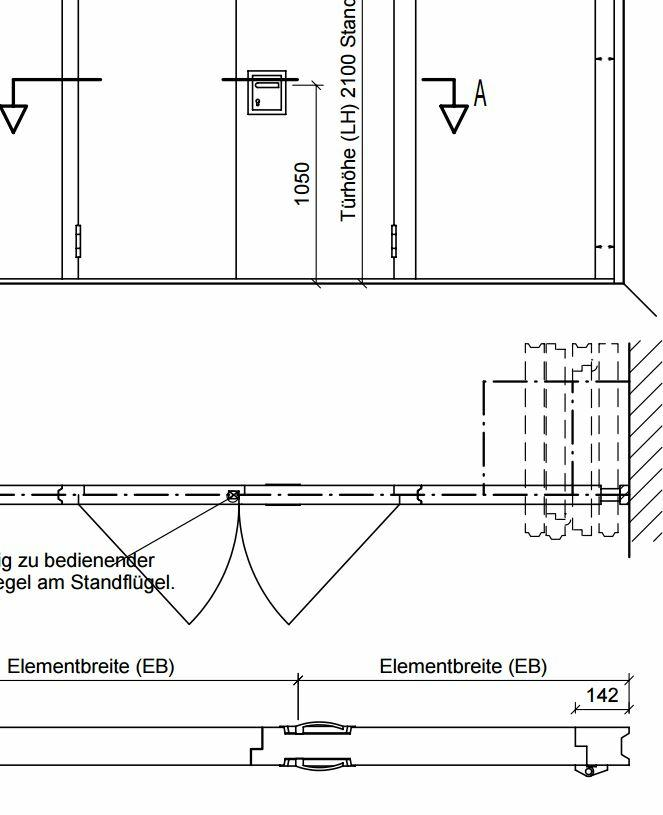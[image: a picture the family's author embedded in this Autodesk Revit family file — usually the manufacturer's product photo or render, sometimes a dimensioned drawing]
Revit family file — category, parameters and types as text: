
# Revit family: Walls_Moving_walls_Komandor_MAW_110_One_single_door_Z1
name_source: partatom
category: Generic Models
revit_build: Autodesk Revit 2014 (Build: 20130308_1515(x64)
units: mm (PartAtom-declared; Revit-internal decimal feet)

## types (1)
- Walls_Moving_walls_Komandor_MAW_110_One_single_door_Z1
    BIMobject category = Folding & Moving Walls
    COBIe Type Category = Wall MOVABLE
    Design country = Poland
    Door Width = 800 mm  [stored 2.62467 ft]
    Edition number = 1
    IFC Classification = Wall
    Installation instructions = http://www.komandorwalls.com
    Manufacturer country = Poland
    Manufacturer name = Komandor
    Masterformat 2014 Code = 07 42 00
    Masterformat 2014 Description = Wall Panels
    Material main = Aluminium
    Material secondary = MDF
    NBS Reference Code = 25-30-20-80
    NBS Reference Description = Sliding Stacking Panel Partition Systems
    Nominal height = 0
    Nominal width = 0
    OmniClass Code = 23-15 13 19
    OmniClass Description = Wall Panels
    Panel Material = Veneer, LF-2
    Product Guid = f88639dd-7851-4d73-ba37-f0ca554d38d5
    Product SKU = maw110
    Product data url = https://bimobject.com
    Product family = Walls
    Product group = MAW
    Profile Material = Komandor_Aluminum
    QR code = http://bimobject.com
    UNSPSC Code = 301615
    Uniclass 1.4 Code = L83122
    Uniclass 1.4 Description = Wall units
    Uniclass 2.0 Code = SS-25-30-20-80
    Uniclass 2.0 Description = Sliding Stacking Panel Partition Systems
    Uniclass 2015 Code = EF_25
    Uniclass 2015 Name = Wall and barrier elements
    Uniformat II Code = C3010
    Uniformat II Description = Wall Finishes
    Weight Net (Kg) = 0
    Youtube clip = https://www.youtube.com

note: [stored X ft] marks values corroborated as IEEE doubles in the binary element streams (Revit-internal decimal feet)

## geometry (parser evidence)
native form markers: Sweep x74
no freeform markers — native parametric forms only
